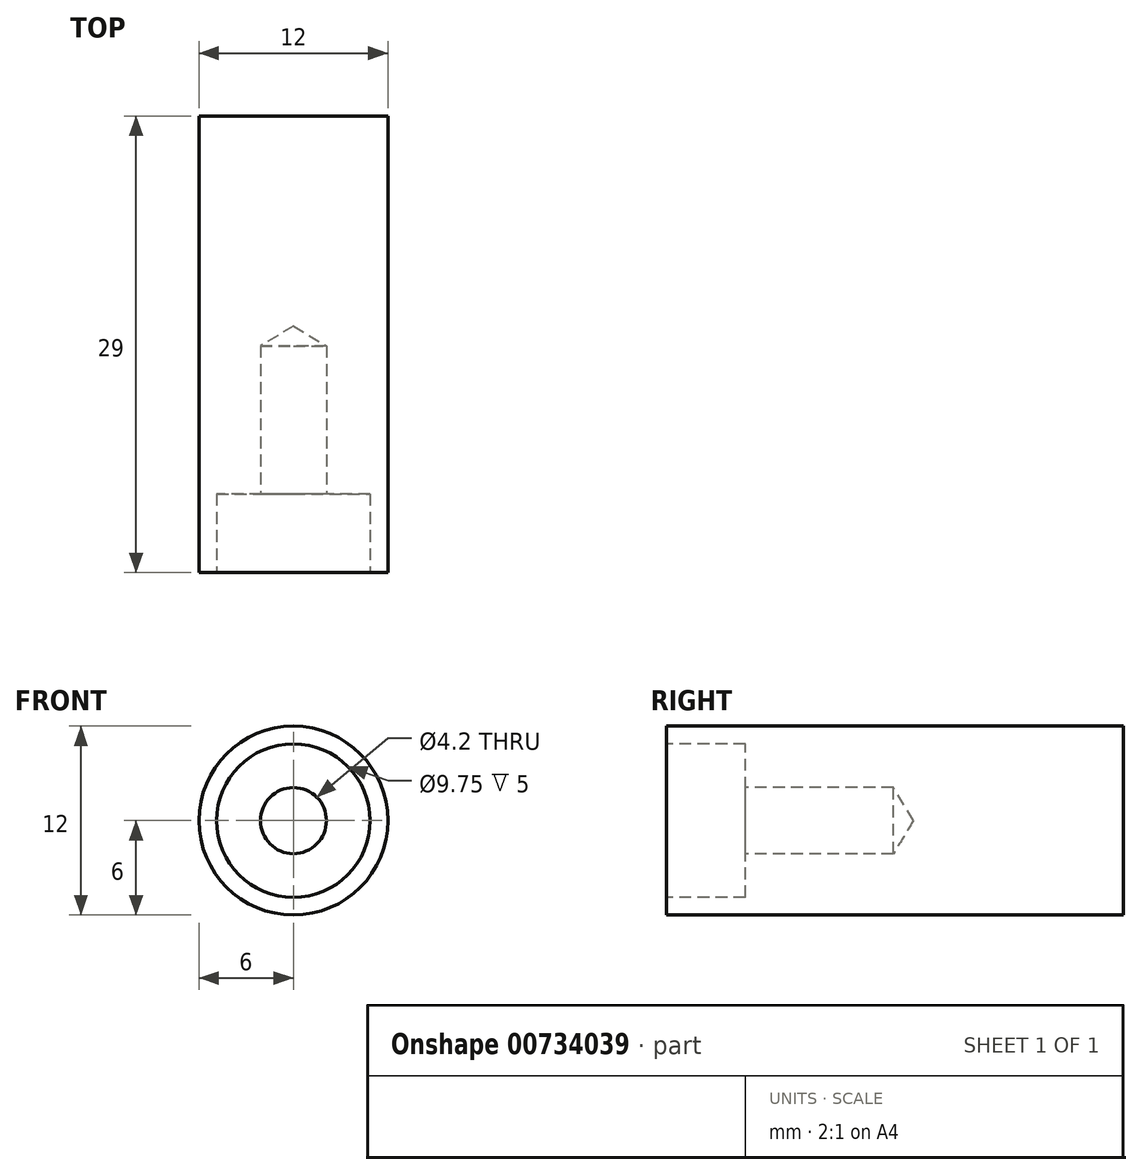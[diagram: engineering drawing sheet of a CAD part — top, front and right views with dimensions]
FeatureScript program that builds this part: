
annotation { "Feature Type Name" : "Feature", "Feature Type Description" : "" }
export const myFeature = defineFeature(function(context is Context, id is Id, definition is map)
    precondition{}
    {
        {
            var Q0;
            Q0=qCreatedBy(makeId("Front.planeOp"),FACE);
            var sketch = newSketch(context, id + "F0", { "sketchPlane" : qUnion([Q0])});
            skCircle(sketch, "E0", {"center": v(0, 0) * mm, "radius": 6 * mm});
            skSolve(sketch);
        }
        {
            var Q0;
            Q0=qSketchRegion(id+"F0",true);
            extrude(context, id + "F1", {"entities" : qUnion([Q0]), "depth" : 29 * mm, "offsetDistance" : 25 * mm});
        }
        {
            var Q0;
            Q0=makeQuery(id+"F1.opExtrude","CAP_FACE",FACE,{"disambiguationData":[OSD([sQuery(id+"F0.wireOp",EDGE,"E0")])],"isStart":false});
            var sketch = newSketch(context, id + "F2", { "sketchPlane" : qUnion([Q0])});
            skPoint(sketch, "E1", {"position": v(0, 0) * mm});
            skSolve(sketch);
        }
        {
            var Q0;
            Q0=sQuery(id+"F2.wireOp",VERTEX,"E1");
            var Q1;
            Q1=makeQuery(id+"F1.opExtrude","SWEPT_BODY",BODY,{"disambiguationData":[OSD([sQuery(id+"F0.wireOp",EDGE,"E0")])]});
            hole(context, id + "F3", {"style" : HoleStyle.C_BORE, "endStyle" : HoleEndStyle.BLIND, "standardTappedOrClearance" : lookupTablePath({ "standard" : "ISO", "engagement" : "75%", "pitch" : "0.8 mm", "size" : "M5", "type" : "Tapped" }), "standardBlindInLast" : lookupTablePath({ "standard" : "ISO", "engagement" : "75%", "pitch" : "0.8 mm", "size" : "M5", "type" : "Tapped" }), "holeDiameter" : 4.2 * mm, "cBoreDiameter" : 9.75 * mm, "cBoreDepth" : 5 * mm, "majorDiameter" : 5 * mm, "showTappedDepth" : true, "holeDepth" : 14.4 * mm, "isTappedThrough" : true, "tappedDepth" : 12 * mm, "tapClearance" : 3, "startFromSketch" : true, "locations" : qUnion([Q0]), "scope" : qUnion([Q1])});
        }
    });
